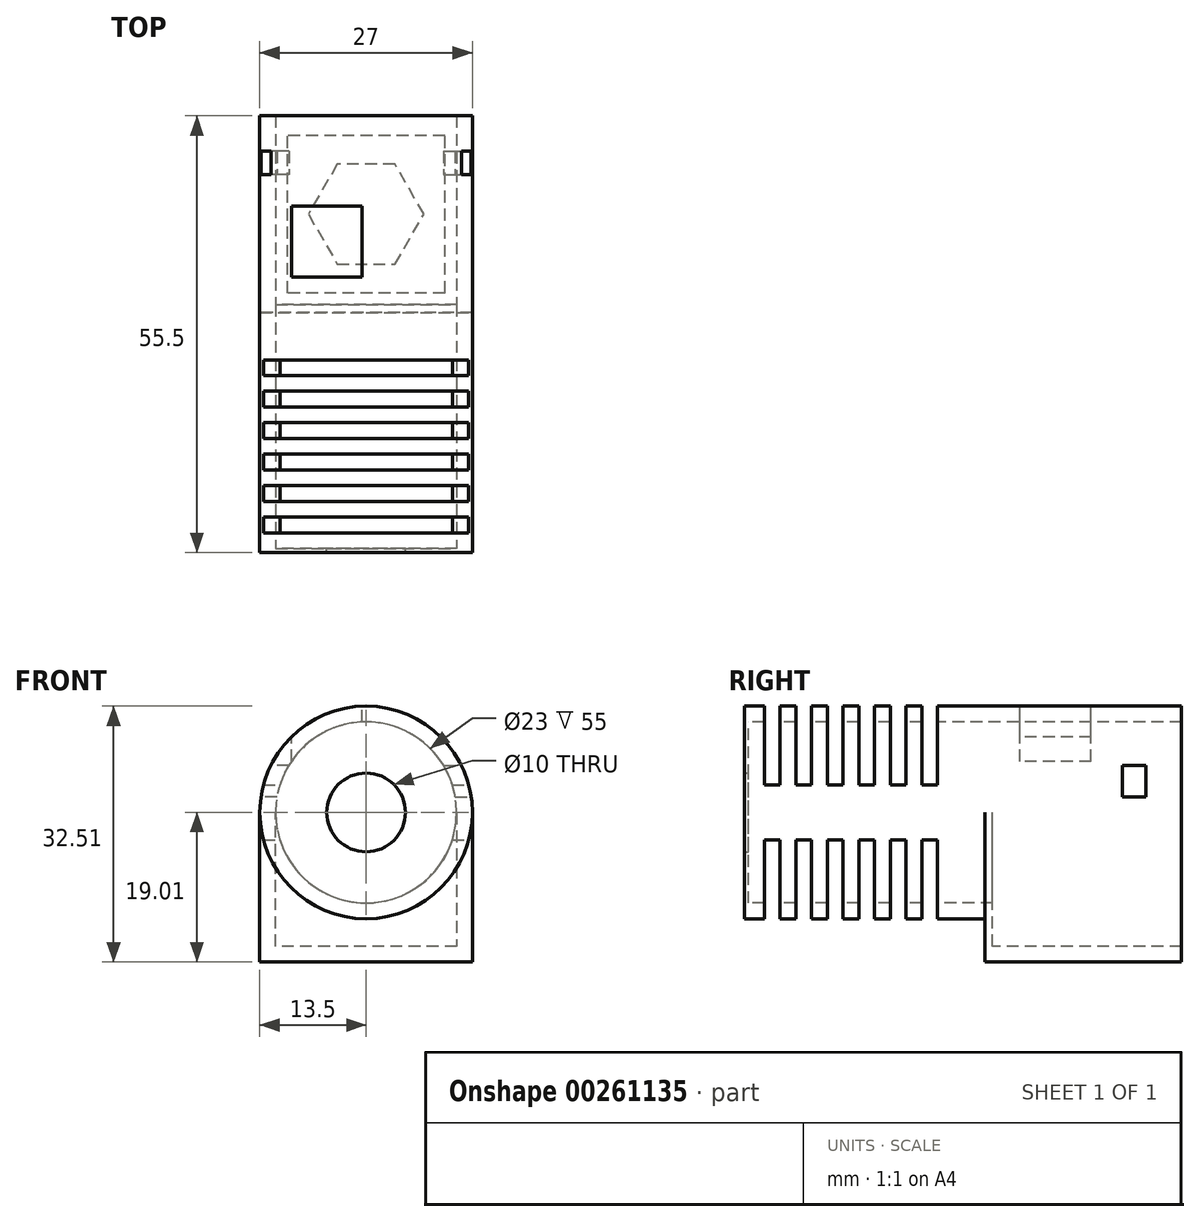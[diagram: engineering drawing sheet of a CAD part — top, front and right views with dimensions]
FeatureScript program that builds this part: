
annotation { "Feature Type Name" : "Feature", "Feature Type Description" : "" }
export const myFeature = defineFeature(function(context is Context, id is Id, definition is map)
    precondition{}
    {
        {
            var Q0;
            Q0=qCreatedBy(makeId("Front.planeOp"),FACE);
            var sketch = newSketch(context, id + "F0", { "sketchPlane" : qUnion([Q0])});
            skCircle(sketch, "E0", {"center": v(0, 0) * mm, "radius": 13.5 * mm});
            skCircle(sketch, "E1", {"center": v(0, 0) * mm, "radius": 11.5 * mm});
            skSolve(sketch);
        }
        {
            var Q0;
            Q0=qSketchRegion(id+"F0",true);
            extrude(context, id + "F1", {"entities" : qUnion([Q0]), "oppositeDirection" : true, "depth" : 30 * mm});
        }
        {
            var Q0;
            Q0=qCreatedBy(makeId("Front.planeOp"),FACE);
            var sketch = newSketch(context, id + "F2", { "sketchPlane" : qUnion([Q0])});
            skCircle(sketch, "E2", {"center": v(0, 0) * mm, "radius": 13.5 * mm});
            skCircle(sketch, "E3", {"center": v(0, 0) * mm, "radius": 5 * mm});
            skSolve(sketch);
        }
        {
            var Q0;
            Q0=qSketchRegion(id+"F2",true);
            extrude(context, id + "F3", {"entities" : qUnion([Q0]), "operationType" : NewBodyOperationType.ADD, "depth" : 0.5 * mm});
        }
        {
            var Q0;
            Q0=qCreatedBy(makeId("Top.planeOp"),FACE);
            cPlane(context, id + "F4", {"entities" : qUnion([Q0]), "cplaneType" : CPlaneType.OFFSET, "offset" : 13.5 * mm, "width" : 150 * mm, "height" : 150 * mm});
        }
        {
            var Q0;
            Q0=qCreatedBy(id+"F4.planeOp",FACE);
            var sketch = newSketch(context, id + "F5", { "sketchPlane" : qUnion([Q0])});
            skLineSegment(sketch, "E4", {"start": v(-13.5, 0) * mm, "end": v(13.5, 0) * mm});
            skLineSegment(sketch, "E5", {"start": v(-13.5, 2) * mm, "end": v(-13.5, 4) * mm});
            skLineSegment(sketch, "E6", {"start": v(-13.5, 26) * mm, "end": v(13.5, 26) * mm});
            skLineSegment(sketch, "E7", {"start": v(13.5, 24) * mm, "end": v(13.5, 22) * mm});
            skLineSegment(sketch, "E8.0.1.0", {"start": v(-13.5, 2) * mm, "end": v(13.5, 2) * mm});
            skLineSegment(sketch, "E8.0.2.0", {"start": v(-13.5, 4) * mm, "end": v(13.5, 4) * mm});
            skLineSegment(sketch, "E8.0.3.0", {"start": v(-13.5, 6) * mm, "end": v(13.5, 6) * mm});
            skLineSegment(sketch, "E8.0.4.0", {"start": v(-13.5, 8) * mm, "end": v(13.5, 8) * mm});
            skLineSegment(sketch, "E8.0.5.0", {"start": v(-13.5, 10) * mm, "end": v(13.5, 10) * mm});
            skLineSegment(sketch, "E8.0.6.0", {"start": v(-13.5, 12) * mm, "end": v(13.5, 12) * mm});
            skLineSegment(sketch, "E8.0.7.0", {"start": v(-13.5, 14) * mm, "end": v(13.5, 14) * mm});
            skLineSegment(sketch, "E8.0.8.0", {"start": v(-13.5, 16) * mm, "end": v(13.5, 16) * mm});
            skLineSegment(sketch, "E8.0.9.0", {"start": v(-13.5, 18) * mm, "end": v(13.5, 18) * mm});
            skLineSegment(sketch, "E8.0.10.0", {"start": v(-13.5, 20) * mm, "end": v(13.5, 20) * mm});
            skLineSegment(sketch, "E8.0.11.0", {"start": v(-13.5, 22) * mm, "end": v(13.5, 22) * mm});
            skLineSegment(sketch, "E8.0.12.0", {"start": v(-13.5, 24) * mm, "end": v(13.5, 24) * mm});
            skLineSegment(sketch, "E9.trimOffspring", {"start": v(-13.5, 22) * mm, "end": v(-13.5, 24) * mm});
            skLineSegment(sketch, "E10.trimOffspring", {"start": v(13.5, 20) * mm, "end": v(13.5, 18) * mm});
            skLineSegment(sketch, "E11.trimOffspring", {"start": v(-13.5, 18) * mm, "end": v(-13.5, 20) * mm});
            skLineSegment(sketch, "E12.trimOffspring", {"start": v(13.5, 16) * mm, "end": v(13.5, 14) * mm});
            skLineSegment(sketch, "E13.trimOffspring", {"start": v(-13.5, 14) * mm, "end": v(-13.5, 16) * mm});
            skLineSegment(sketch, "E14.trimOffspring", {"start": v(13.5, 12) * mm, "end": v(13.5, 10) * mm});
            skLineSegment(sketch, "E15.trimOffspring", {"start": v(-13.5, 10) * mm, "end": v(-13.5, 12) * mm});
            skLineSegment(sketch, "E16.trimOffspring", {"start": v(13.5, 8) * mm, "end": v(13.5, 6) * mm});
            skLineSegment(sketch, "E17.trimOffspring", {"start": v(-13.5, 6) * mm, "end": v(-13.5, 8) * mm});
            skLineSegment(sketch, "E18.trimOffspring", {"start": v(13.5, 4) * mm, "end": v(13.5, 2) * mm});
            skLineSegment(sketch, "E19", {"start": v(0, -4) * mm, "end": v(0, -5) * mm});
            skSolve(sketch);
        }
        {
            var Q0;
            Q0=qSketchRegion(id+"F5",true);
            extrude(context, id + "F6", {"entities" : qUnion([Q0]), "operationType" : NewBodyOperationType.REMOVE, "oppositeDirection" : true, "depth" : 10 * mm});
        }
        {
            var Q0;
            Q0=qCreatedBy(makeId("Top.planeOp"),FACE);
            cPlane(context, id + "F7", {"entities" : qUnion([Q0]), "cplaneType" : CPlaneType.OFFSET, "offset" : 13.5 * mm, "oppositeDirection" : true, "width" : 150 * mm, "height" : 150 * mm});
        }
        {
            var Q0;
            Q0=qCreatedBy(id+"F7.planeOp",FACE);
            var sketch = newSketch(context, id + "F8", { "sketchPlane" : qUnion([Q0])});
            skLineSegment(sketch, "E20", {"start": v(13.5, 2) * mm, "end": v(13.5, 4) * mm});
            skLineSegment(sketch, "E21", {"start": v(-13.5, 2) * mm, "end": v(-13.5, 4) * mm});
            skLineSegment(sketch, "E22.0.1.0", {"start": v(-13.5, 2) * mm, "end": v(13.5, 2) * mm});
            skLineSegment(sketch, "E22.0.2.0", {"start": v(-13.5, 4) * mm, "end": v(13.5, 4) * mm});
            skLineSegment(sketch, "E22.0.3.0", {"start": v(-13.5, 6) * mm, "end": v(13.5, 6) * mm});
            skLineSegment(sketch, "E22.0.4.0", {"start": v(-13.5, 8) * mm, "end": v(13.5, 8) * mm});
            skLineSegment(sketch, "E22.0.5.0", {"start": v(-13.5, 10) * mm, "end": v(13.5, 10) * mm});
            skLineSegment(sketch, "E22.0.6.0", {"start": v(-13.5, 12) * mm, "end": v(13.5, 12) * mm});
            skLineSegment(sketch, "E22.0.7.0", {"start": v(-13.5, 14) * mm, "end": v(13.5, 14) * mm});
            skLineSegment(sketch, "E22.0.8.0", {"start": v(-13.5, 16) * mm, "end": v(13.5, 16) * mm});
            skLineSegment(sketch, "E22.0.9.0", {"start": v(-13.5, 18) * mm, "end": v(13.5, 18) * mm});
            skLineSegment(sketch, "E22.0.10.0", {"start": v(-13.5, 20) * mm, "end": v(13.5, 20) * mm});
            skLineSegment(sketch, "E22.0.11.0", {"start": v(-13.5, 22) * mm, "end": v(13.5, 22) * mm});
            skLineSegment(sketch, "E22.0.12.0", {"start": v(-13.5, 24) * mm, "end": v(13.5, 24) * mm});
            skLineSegment(sketch, "E23.trimOffspring", {"start": v(-13.5, 6) * mm, "end": v(-13.5, 8) * mm});
            skLineSegment(sketch, "E24.trimOffspring", {"start": v(13.5, 6) * mm, "end": v(13.5, 8) * mm});
            skLineSegment(sketch, "E25.trimOffspring", {"start": v(-13.5, 4) * mm, "end": v(-13.5, 2) * mm});
            skLineSegment(sketch, "E26.trimOffspring", {"start": v(-13.5, 8) * mm, "end": v(-13.5, 6) * mm});
            skLineSegment(sketch, "E27.trimOffspring", {"start": v(-13.5, 10) * mm, "end": v(-13.5, 12) * mm});
            skLineSegment(sketch, "E28.trimOffspring", {"start": v(13.5, 10) * mm, "end": v(13.5, 12) * mm});
            skLineSegment(sketch, "E29.trimOffspring", {"start": v(-13.5, 12) * mm, "end": v(-13.5, 10) * mm});
            skLineSegment(sketch, "E30.trimOffspring", {"start": v(-13.5, 14) * mm, "end": v(-13.5, 16) * mm});
            skLineSegment(sketch, "E31.trimOffspring", {"start": v(13.5, 14) * mm, "end": v(13.5, 16) * mm});
            skLineSegment(sketch, "E32.trimOffspring", {"start": v(-13.5, 16) * mm, "end": v(-13.5, 14) * mm});
            skLineSegment(sketch, "E33.trimOffspring", {"start": v(13.5, 18) * mm, "end": v(13.5, 20) * mm});
            skLineSegment(sketch, "E34.trimOffspring", {"start": v(-13.5, 20) * mm, "end": v(-13.5, 18) * mm});
            skLineSegment(sketch, "E35.trimOffspring", {"start": v(-13.5, 22) * mm, "end": v(-13.5, 24) * mm});
            skLineSegment(sketch, "E36.trimOffspring", {"start": v(13.5, 22) * mm, "end": v(13.5, 24) * mm});
            skLineSegment(sketch, "E37.trimOffspring", {"start": v(-13.5, 24) * mm, "end": v(-13.5, 22) * mm});
            skSolve(sketch);
        }
        {
            var Q0;
            Q0=qSketchRegion(id+"F8",true);
            extrude(context, id + "F9", {"entities" : qUnion([Q0]), "operationType" : NewBodyOperationType.REMOVE, "depth" : 10 * mm});
        }
        {
            var Q0;
            Q0=makeQuery(id+"F1.opExtrude","CAP_FACE",FACE,{"disambiguationData":[OSD([sQuery(id+"F0.wireOp",EDGE,"E0"),sQuery(id+"F0.wireOp",EDGE,"E1")])],"isStart":false});
            var sketch = newSketch(context, id + "F10", { "sketchPlane" : qUnion([Q0])});
            skArc(sketch, "E38", {"start": v(11.5, -7.07) * mm, "mid": v(0, 13.5) * mm, "end": v(-11.5, -7.07) * mm});
            skLineSegment(sketch, "E39", {"start": v(-13.5, 0) * mm, "end": v(-13.5, -19) * mm});
            skLineSegment(sketch, "E40", {"start": v(-13.5, -19) * mm, "end": v(13.5, -19) * mm});
            skLineSegment(sketch, "E41", {"start": v(13.5, -19) * mm, "end": v(13.5, 0) * mm});
            skLineSegment(sketch, "E42", {"start": v(-11.5, 0) * mm, "end": v(-11.5, -17) * mm});
            skLineSegment(sketch, "E43", {"start": v(-11.5, -17) * mm, "end": v(11.5, -17) * mm});
            skLineSegment(sketch, "E44", {"start": v(11.5, -17) * mm, "end": v(11.5, 0) * mm});
            skCircle(sketch, "E45", {"center": v(0, 0) * mm, "radius": 11.5 * mm});
            skSolve(sketch);
        }
        {
            var Q0;
            {var subQ0=sQuery(id+"F10.wireOp",EDGE,"E38");var subQ1=makeQuery(id+"F10.imprint","INTERSECT",VERTEX,{"derivedFrom":[subQ0,sQuery(id+"F10.wireOp",EDGE,"E39")]});Q0=makeQuery(id+"F10.imprint","IMPRINT",FACE,{"disambiguationData":[TD([[makeQuery(id+"F10.imprint","IMPRINT",EDGE,{"disambiguationData":[TD([[subQ1,-1.0]])],"derivedFrom":subQ0}),-1.0]])]});}
            var Q1;
            {var subQ0=sQuery(id+"F10.wireOp",EDGE,"E39");Q1=makeQuery(id+"F10.imprint","IMPRINT",FACE,{"disambiguationData":[TD([[makeQuery(id+"F10.imprint","IMPRINT",EDGE,{"derivedFrom":subQ0}),1.0]])]});}
            extrude(context, id + "F11", {"entities" : qUnion([Q0, Q1]), "operationType" : NewBodyOperationType.ADD, "depth" : 25 * mm});
        }
        {
            var Q0;
            Q0=makeQuery(id+"F1.opExtrude","CAP_FACE",FACE,{"disambiguationData":[OSD([sQuery(id+"F0.wireOp",EDGE,"E0"),sQuery(id+"F0.wireOp",EDGE,"E1")])],"isStart":false});
            var sketch = newSketch(context, id + "F12", { "sketchPlane" : qUnion([Q0])});
            skCircle(sketch, "E46", {"center": v(0, 0) * mm, "radius": 13.5 * mm});
            skLineSegment(sketch, "E47", {"start": v(-13.5, 0) * mm, "end": v(-13.5, -19) * mm});
            skLineSegment(sketch, "E48", {"start": v(-13.5, -19) * mm, "end": v(13.5, -19) * mm});
            skLineSegment(sketch, "E49", {"start": v(13.5, -19) * mm, "end": v(13.5, 0) * mm});
            skSolve(sketch);
        }
        {
            var Q0;
            {var subQ0=sQuery(id+"F12.wireOp",EDGE,"E47");Q0=makeQuery(id+"F12.imprint","IMPRINT",FACE,{"disambiguationData":[TD([[makeQuery(id+"F12.imprint","IMPRINT",EDGE,{"derivedFrom":subQ0}),1.0]])]});}
            var Q1;
            {var subQ1=sQuery(id+"F0.wireOp",EDGE,"E1");Q1=makeQuery(id+"F12.imprint","IMPRINT",FACE,{"disambiguationData":[TD([[makeQuery(id+"F12.imprint","IMPRINT",EDGE,{"derivedFrom":makeQuery(id+"F1.opExtrude","CAP_EDGE",EDGE,{"disambiguationData":[OSD([subQ1])],"isStart":false})}),1.0]])]});}
            extrude(context, id + "F13", {"entities" : qUnion([Q0, Q1]), "operationType" : NewBodyOperationType.ADD, "depth" : 1 * mm});
        }
        {
            var Q0;
            Q0=makeQuery(id+"F11.opExtrude","SWEPT_FACE",FACE,{"disambiguationData":[OSD([sQuery(id+"F10.wireOp",EDGE,"E40")])]});
            var sketch = newSketch(context, id + "F14", { "sketchPlane" : qUnion([Q0])});
            skCircle(sketch, "E50.cCircle", {"center": v(0, -42.5) * mm, "radius": 6.35 * mm, "construction": true});
            skLineSegment(sketch, "E50.0", {"start": v(3.67, -36.15) * mm, "end": v(7.33, -42.5) * mm});
            skLineSegment(sketch, "E50.1", {"start": v(7.33, -42.5) * mm, "end": v(3.67, -48.85) * mm});
            skLineSegment(sketch, "E50.2", {"start": v(3.67, -48.85) * mm, "end": v(-3.67, -48.85) * mm});
            skLineSegment(sketch, "E50.3", {"start": v(-3.67, -48.85) * mm, "end": v(-7.33, -42.5) * mm});
            skLineSegment(sketch, "E50.4", {"start": v(-7.33, -42.5) * mm, "end": v(-3.67, -36.15) * mm});
            skLineSegment(sketch, "E50.5", {"start": v(-3.67, -36.15) * mm, "end": v(3.67, -36.15) * mm});
            skPoint(sketch, "E50.0.midPoint", {"position": v(5.5, -39.32) * mm});
            skPoint(sketch, "E51", {"position": v(-13.5, -30) * mm});
            skPoint(sketch, "E52", {"position": v(-13.5, -55) * mm});
            skLineSegment(sketch, "E53.bottom", {"start": v(10, -32.5) * mm, "end": v(-10, -32.5) * mm});
            skLineSegment(sketch, "E53.top", {"start": v(10, -52.5) * mm, "end": v(-10, -52.5) * mm});
            skLineSegment(sketch, "E53.left", {"start": v(10, -32.5) * mm, "end": v(10, -52.5) * mm});
            skLineSegment(sketch, "E53.right", {"start": v(-10, -32.5) * mm, "end": v(-10, -52.5) * mm});
            skSolve(sketch);
        }
        {
            var Q0;
            Q0=qSketchRegion(id+"F14",true);
            extrude(context, id + "F15", {"entities" : qUnion([Q0]), "operationType" : NewBodyOperationType.ADD, "depth" : 7 / 812.8 * mm});
        }
        {
            var Q0;
            Q0=makeQuery(id+"F11.opExtrude","SWEPT_FACE",FACE,{"disambiguationData":[OSD([sQuery(id+"F10.wireOp",EDGE,"E39")])]});
            var sketch = newSketch(context, id + "F16", { "sketchPlane" : qUnion([Q0])});
            skLineSegment(sketch, "E54.bottom", {"start": v(50.5, 2) * mm, "end": v(47.5, 2) * mm});
            skLineSegment(sketch, "E54.top", {"start": v(50.5, 6) * mm, "end": v(47.5, 6) * mm});
            skLineSegment(sketch, "E54.left", {"start": v(50.5, 2) * mm, "end": v(50.5, 6) * mm});
            skLineSegment(sketch, "E54.right", {"start": v(47.5, 2) * mm, "end": v(47.5, 6) * mm});
            skPoint(sketch, "E54.middle", {"position": v(49, 4) * mm});
            skSolve(sketch);
        }
        {
            var Q0;
            Q0=qSketchRegion(id+"F16",true);
            extrude(context, id + "F17", {"entities" : qUnion([Q0]), "operationType" : NewBodyOperationType.REMOVE, "oppositeDirection" : true, "depth" : 4 * mm});
        }
        {
            var Q0;
            Q0=makeQuery(id+"F11.opExtrude","SWEPT_FACE",FACE,{"disambiguationData":[OSD([sQuery(id+"F10.wireOp",EDGE,"E41")])]});
            var sketch = newSketch(context, id + "F18", { "sketchPlane" : qUnion([Q0])});
            skLineSegment(sketch, "E55.bottom", {"start": v(-47.5, 2) * mm, "end": v(-50.5, 2) * mm});
            skLineSegment(sketch, "E55.top", {"start": v(-47.5, 6) * mm, "end": v(-50.5, 6) * mm});
            skLineSegment(sketch, "E55.left", {"start": v(-47.5, 2) * mm, "end": v(-47.5, 6) * mm});
            skLineSegment(sketch, "E55.right", {"start": v(-50.5, 2) * mm, "end": v(-50.5, 6) * mm});
            skPoint(sketch, "E55.middle", {"position": v(-49, 4) * mm});
            skSolve(sketch);
        }
        {
            var Q0;
            Q0=makeQuery(id+"F18.imprint","IMPRINT",FACE,{"disambiguationData":[TD([[makeQuery(id+"F18.imprint","IMPRINT",EDGE,{"derivedFrom":sQuery(id+"F18.wireOp",EDGE,"E55.bottom")}),-1.0]])]});
            extrude(context, id + "F19", {"entities" : qUnion([Q0]), "operationType" : NewBodyOperationType.REMOVE, "oppositeDirection" : true, "depth" : 4 * mm});
        }
        {
            var Q0;
            Q0=qCreatedBy(id+"F4.planeOp",FACE);
            var sketch = newSketch(context, id + "F20", { "sketchPlane" : qUnion([Q0])});
            skLineSegment(sketch, "E56.bottom", {"start": v(-0.5, 43.5) * mm, "end": v(-9.5, 43.5) * mm});
            skLineSegment(sketch, "E56.top", {"start": v(-0.5, 34.5) * mm, "end": v(-9.5, 34.5) * mm});
            skLineSegment(sketch, "E56.left", {"start": v(-0.5, 43.5) * mm, "end": v(-0.5, 34.5) * mm});
            skLineSegment(sketch, "E56.right", {"start": v(-9.5, 43.5) * mm, "end": v(-9.5, 34.5) * mm});
            skPoint(sketch, "E56.middle", {"position": v(-5, 39) * mm});
            skSolve(sketch);
        }
        {
            var Q0;
            Q0=makeQuery(id+"F20.imprint","IMPRINT",FACE,{"disambiguationData":[TD([[makeQuery(id+"F20.imprint","IMPRINT",EDGE,{"derivedFrom":sQuery(id+"F20.wireOp",EDGE,"E56.bottom")}),1.0]])]});
            extrude(context, id + "F21", {"entities" : qUnion([Q0]), "operationType" : NewBodyOperationType.REMOVE, "oppositeDirection" : true, "depth" : 8 * mm});
        }
    });
